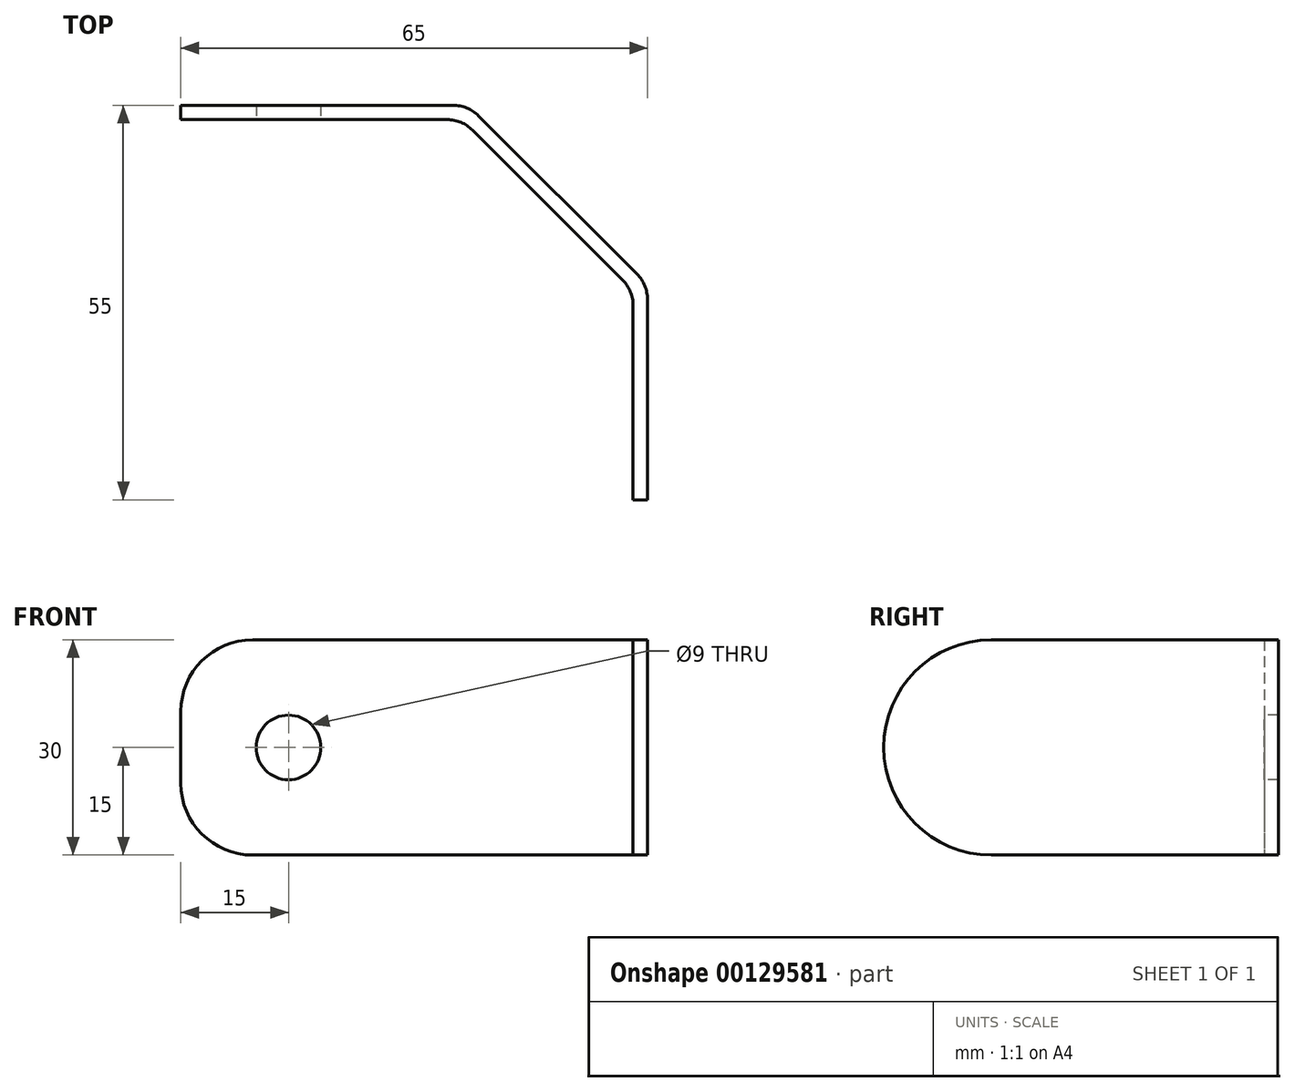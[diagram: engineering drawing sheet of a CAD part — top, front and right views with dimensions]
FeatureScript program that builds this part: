
annotation { "Feature Type Name" : "Feature", "Feature Type Description" : "" }
export const myFeature = defineFeature(function(context is Context, id is Id, definition is map)
    precondition{}
    {
        {
            var Q0;
            Q0=qCreatedBy(makeId("Top.planeOp"),FACE);
            var sketch = newSketch(context, id + "F0", { "sketchPlane" : qUnion([Q0])});
            skLineSegment(sketch, "E0", {"start": v(-100, 0) * mm, "end": v(100, 0) * mm, "construction": true});
            skLineSegment(sketch, "E1", {"start": v(-102.07, 0) * mm, "end": v(-140, 0) * mm});
            skLineSegment(sketch, "E2", {"start": v(100, 0) * mm, "end": v(140, 0) * mm, "construction": true});
            skLineSegment(sketch, "E3", {"start": v(0, 0) * mm, "end": v(0, -55) * mm, "construction": true});
            skLineSegment(sketch, "E4", {"start": v(-98.54, -1.46) * mm, "end": v(-76.46, -23.54) * mm});
            skLineSegment(sketch, "E5", {"start": v(-75, -27.07) * mm, "end": v(-75, -55) * mm});
            skLineSegment(sketch, "E6", {"start": v(-75, -55) * mm, "end": v(75, -55) * mm, "construction": true});
            skLineSegment(sketch, "E7", {"start": v(-75, -55) * mm, "end": v(-77, -55) * mm});
            skLineSegment(sketch, "E8", {"start": v(-140, -2) * mm, "end": v(-140, 0) * mm});
            skPoint(sketch, "E9.visualSharp", {"position": v(-100, 0) * mm});
            skArc(sketch, "E9.filletArc", {"start": v(-98.54, -1.46) * mm, "mid": v(-100.16, -0.38) * mm, "end": v(-102.07, 0) * mm});
            skPoint(sketch, "E10.visualSharp", {"position": v(-75, -25) * mm});
            skArc(sketch, "E10.filletArc", {"start": v(-75, -27.07) * mm, "mid": v(-75.38, -25.16) * mm, "end": v(-76.46, -23.54) * mm});
            skLineSegment(sketch, "E11.0", {"start": v(-102.9, -2) * mm, "end": v(-140, -2) * mm});
            skLineSegment(sketch, "E11.1", {"start": v(-99.36, -3.46) * mm, "end": v(-78.46, -24.36) * mm});
            skLineSegment(sketch, "E11.2", {"start": v(-77, -27.9) * mm, "end": v(-77, -55) * mm});
            skPoint(sketch, "E12.visualSharp", {"position": v(-100.83, -2) * mm});
            skArc(sketch, "E12.filletArc", {"start": v(-99.36, -3.46) * mm, "mid": v(-100.99, -2.38) * mm, "end": v(-102.9, -2) * mm});
            skPoint(sketch, "E13.visualSharp", {"position": v(-77, -25.83) * mm});
            skArc(sketch, "E13.filletArc", {"start": v(-77, -27.9) * mm, "mid": v(-77.38, -25.99) * mm, "end": v(-78.46, -24.36) * mm});
            skSolve(sketch);
        }
        {
            var Q0;
            Q0 = qSketchRegion(id + "F0", true);
            extrude(context, id + "F1", {"entities" : qUnion([Q0]), "endBound" : BoundingType.SYMMETRIC, "depth" : 30 * mm});
        }
        {
            var Q0;
            Q0=makeQuery(id+"F1.opExtrude","CAP_EDGE",EDGE,{"disambiguationData":[OSD([sQuery(id+"F0.wireOp",EDGE,"E7")])],"isStart":false});
            var Q1;
            Q1=makeQuery(id+"F1.opExtrude","CAP_EDGE",EDGE,{"disambiguationData":[OSD([sQuery(id+"F0.wireOp",EDGE,"E7")])],"isStart":true});
            fillet(context, id + "F2", {"entities" : qUnion([Q0, Q1]), "radius" : 15 * mm, "tangentPropagation" : true, "allowEdgeOverflow" : false});
        }
        {
            var Q0;
            Q0=makeQuery(id+"F1.opExtrude","SWEPT_FACE",FACE,{"disambiguationData":[OSD([sQuery(id+"F0.wireOp",EDGE,"E11.0")])]});
            var sketch = newSketch(context, id + "F3", { "sketchPlane" : qUnion([Q0])});
            skCircle(sketch, "E14", {"center": v(-125, 0) * mm, "radius": 4.5 * mm});
            skSolve(sketch);
        }
        {
            var Q0;
            Q0 = qSketchRegion(id + "F3", true);
            extrude(context, id + "F4", {"entities" : qUnion([Q0]), "operationType" : NewBodyOperationType.REMOVE, "endBound" : BoundingType.THROUGH_ALL, "oppositeDirection" : true, "depth" : 25.4 * mm});
        }
        {
            var Q0;
            Q0=makeQuery(id+"F1.opExtrude","CAP_EDGE",EDGE,{"disambiguationData":[OSD([sQuery(id+"F0.wireOp",EDGE,"E8")])],"isStart":false});
            var Q1;
            Q1=makeQuery(id+"F1.opExtrude","CAP_EDGE",EDGE,{"disambiguationData":[OSD([sQuery(id+"F0.wireOp",EDGE,"E8")])],"isStart":true});
            fillet(context, id + "F5", {"entities" : qUnion([Q0, Q1]), "radius" : 10 * mm, "tangentPropagation" : true, "allowEdgeOverflow" : false});
        }
    });
